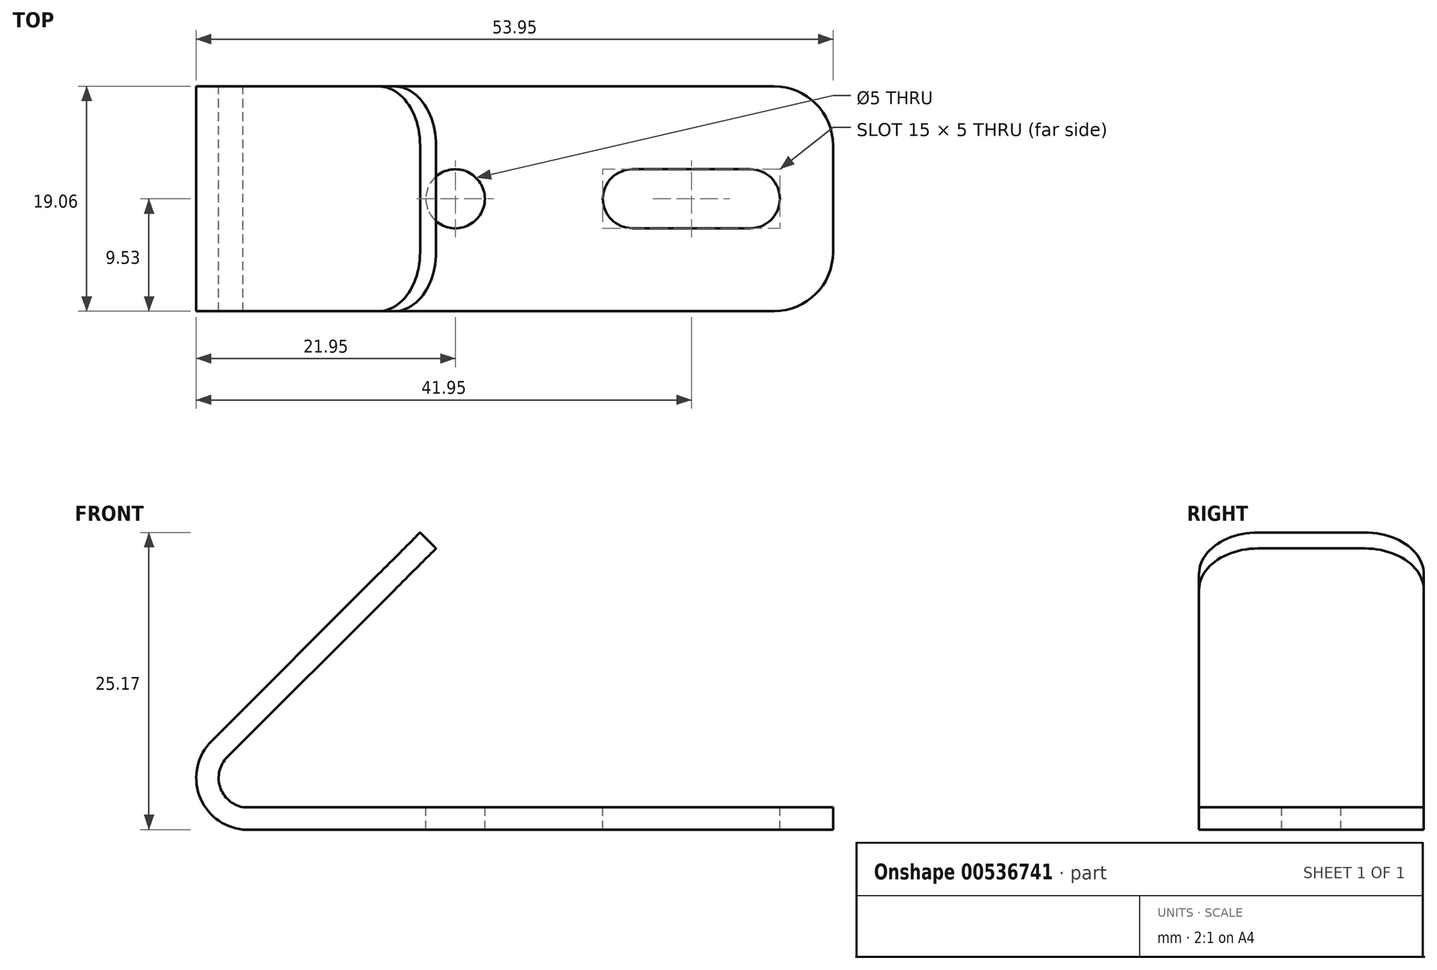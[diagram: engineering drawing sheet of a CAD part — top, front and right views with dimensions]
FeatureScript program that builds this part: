
annotation { "Feature Type Name" : "Feature", "Feature Type Description" : "" }
export const myFeature = defineFeature(function(context is Context, id is Id, definition is map)
    precondition{}
    {
        {
            var Q0;
            Q0=qCreatedBy(makeId("Front.planeOp"),FACE);
            var sketch = newSketch(context, id + "F0", { "sketchPlane" : qUnion([Q0])});
            skLineSegment(sketch, "E0", {"start": v(0, 0) * mm, "end": v(-50, 0) * mm});
            skLineSegment(sketch, "E1", {"start": v(0, 0) * mm, "end": v(0, 1.9) * mm});
            skLineSegment(sketch, "E2", {"start": v(-52.66, 7.49) * mm, "end": v(-34.99, 25.17) * mm});
            skArc(sketch, "E3", {"start": v(-52.66, 7.49) * mm, "mid": v(-53.7, 2.9) * mm, "end": v(-50, 0) * mm});
            skLineSegment(sketch, "E4", {"start": v(0, 1.9) * mm, "end": v(-50, 1.9) * mm});
            skLineSegment(sketch, "E5", {"start": v(-34.99, 25.17) * mm, "end": v(-33.64, 23.82) * mm});
            skLineSegment(sketch, "E6", {"start": v(-33.64, 23.82) * mm, "end": v(-51.32, 6.14) * mm});
            skArc(sketch, "E7", {"start": v(-51.32, 6.14) * mm, "mid": v(-51.94, 3.62) * mm, "end": v(-50, 1.9) * mm});
            skSolve(sketch);
        }
        {
            var Q0;
            Q0 = qSketchRegion(id + "F0", true);
            extrude(context, id + "F1", {"entities" : qUnion([Q0]), "endBound" : BoundingType.SYMMETRIC, "depth" : 19.05 * mm, "offsetDistance" : 25 * mm});
        }
        {
            var Q0;
            Q0=makeQuery(id+"F1.opExtrude","SWEPT_FACE",FACE,{"disambiguationData":[OSD([sQuery(id+"F0.wireOp",EDGE,"E2")])]});
            var sketch = newSketch(context, id + "F2", { "sketchPlane" : qUnion([Q0])});
            skCircle(sketch, "E8", {"center": v(-14.44, -5.03) * mm, "radius": 1.5 * mm});
            skCircle(sketch, "E9.MirrorC", {"center": v(14.44, -5.03) * mm, "radius": 1.5 * mm});
            skSolve(sketch);
        }
        {
            var Q0;
            Q0=makeQuery(id+"F2.imprint","IMPRINT",FACE,{"disambiguationData":[TD([[makeQuery(id+"F2.imprint","IMPRINT",EDGE,{"derivedFrom":sQuery(id+"F2.wireOp",EDGE,"E9.MirrorC")}),-1.0]])]});
            var Q1;
            Q1=makeQuery(id+"F2.imprint","IMPRINT",FACE,{"disambiguationData":[TD([[makeQuery(id+"F2.imprint","IMPRINT",EDGE,{"derivedFrom":sQuery(id+"F2.wireOp",EDGE,"E8")}),1.0]])]});
            var Q2;
            Q2=makeQuery(id+"F1.opExtrude","SWEPT_FACE",FACE,{"disambiguationData":[OSD([sQuery(id+"F0.wireOp",EDGE,"E6")])]});
            extrude(context, id + "F3", {"entities" : qUnion([Q0, Q1]), "operationType" : NewBodyOperationType.REMOVE, "endBound" : BoundingType.UP_TO_SURFACE, "oppositeDirection" : true, "depth" : 25 * mm, "endBoundEntityFace" : qUnion([Q2]), "offsetDistance" : 25 * mm});
        }
        {
            var Q0;
            Q0=makeQuery(id+"F1.opExtrude","SWEPT_FACE",FACE,{"disambiguationData":[OSD([sQuery(id+"F0.wireOp",EDGE,"E4")])]});
            var sketch = newSketch(context, id + "F4", { "sketchPlane" : qUnion([Q0])});
            skCircle(sketch, "E10", {"center": v(-32, 0) * mm, "radius": 2.5 * mm});
            skArc(sketch, "E11", {"start": v(-17, 2.5) * mm, "mid": v(-19.5, 0) * mm, "end": v(-17, -2.5) * mm});
            skArc(sketch, "E12", {"start": v(-7, -2.5) * mm, "mid": v(-4.5, 0) * mm, "end": v(-7, 2.5) * mm});
            skLineSegment(sketch, "E13", {"start": v(-17, -2.5) * mm, "end": v(-7, -2.5) * mm});
            skLineSegment(sketch, "E14", {"start": v(-17, 2.5) * mm, "end": v(-7, 2.5) * mm});
            skSolve(sketch);
        }
        {
            var Q0;
            Q0=makeQuery(id+"F4.imprint","IMPRINT",FACE,{"disambiguationData":[TD([[makeQuery(id+"F4.imprint","IMPRINT",EDGE,{"derivedFrom":sQuery(id+"F4.wireOp",EDGE,"E10")}),1.0]])]});
            var Q1;
            Q1=makeQuery(id+"F4.imprint","IMPRINT",FACE,{"disambiguationData":[TD([[makeQuery(id+"F4.imprint","IMPRINT",EDGE,{"derivedFrom":sQuery(id+"F4.wireOp",EDGE,"E11")}),1.0]])]});
            var Q2;
            Q2=makeQuery(id+"F1.opExtrude","SWEPT_FACE",FACE,{"disambiguationData":[OSD([sQuery(id+"F0.wireOp",EDGE,"E0")])]});
            extrude(context, id + "F5", {"entities" : qUnion([Q0, Q1]), "operationType" : NewBodyOperationType.REMOVE, "endBound" : BoundingType.UP_TO_SURFACE, "oppositeDirection" : true, "depth" : 25 * mm, "endBoundEntityFace" : qUnion([Q2]), "offsetDistance" : 25 * mm});
        }
        {
            var Q0;
            Q0=makeQuery(id+"F1.opExtrude","CAP_EDGE",EDGE,{"disambiguationData":[OSD([sQuery(id+"F0.wireOp",EDGE,"E5")])],"isStart":false});
            var Q1;
            Q1=makeQuery(id+"F1.opExtrude","CAP_EDGE",EDGE,{"disambiguationData":[OSD([sQuery(id+"F0.wireOp",EDGE,"E5")])],"isStart":true});
            var Q2;
            Q2=makeQuery(id+"F1.opExtrude","CAP_EDGE",EDGE,{"disambiguationData":[OSD([sQuery(id+"F0.wireOp",EDGE,"E1")])],"isStart":true});
            var Q3;
            Q3=makeQuery(id+"F1.opExtrude","CAP_EDGE",EDGE,{"disambiguationData":[OSD([sQuery(id+"F0.wireOp",EDGE,"E1")])],"isStart":false});
            fillet(context, id + "F6", {"entities" : qUnion([Q0, Q1, Q2, Q3]), "radius" : 5 * mm, "tangentPropagation" : true, "allowEdgeOverflow" : false});
        }
    });
